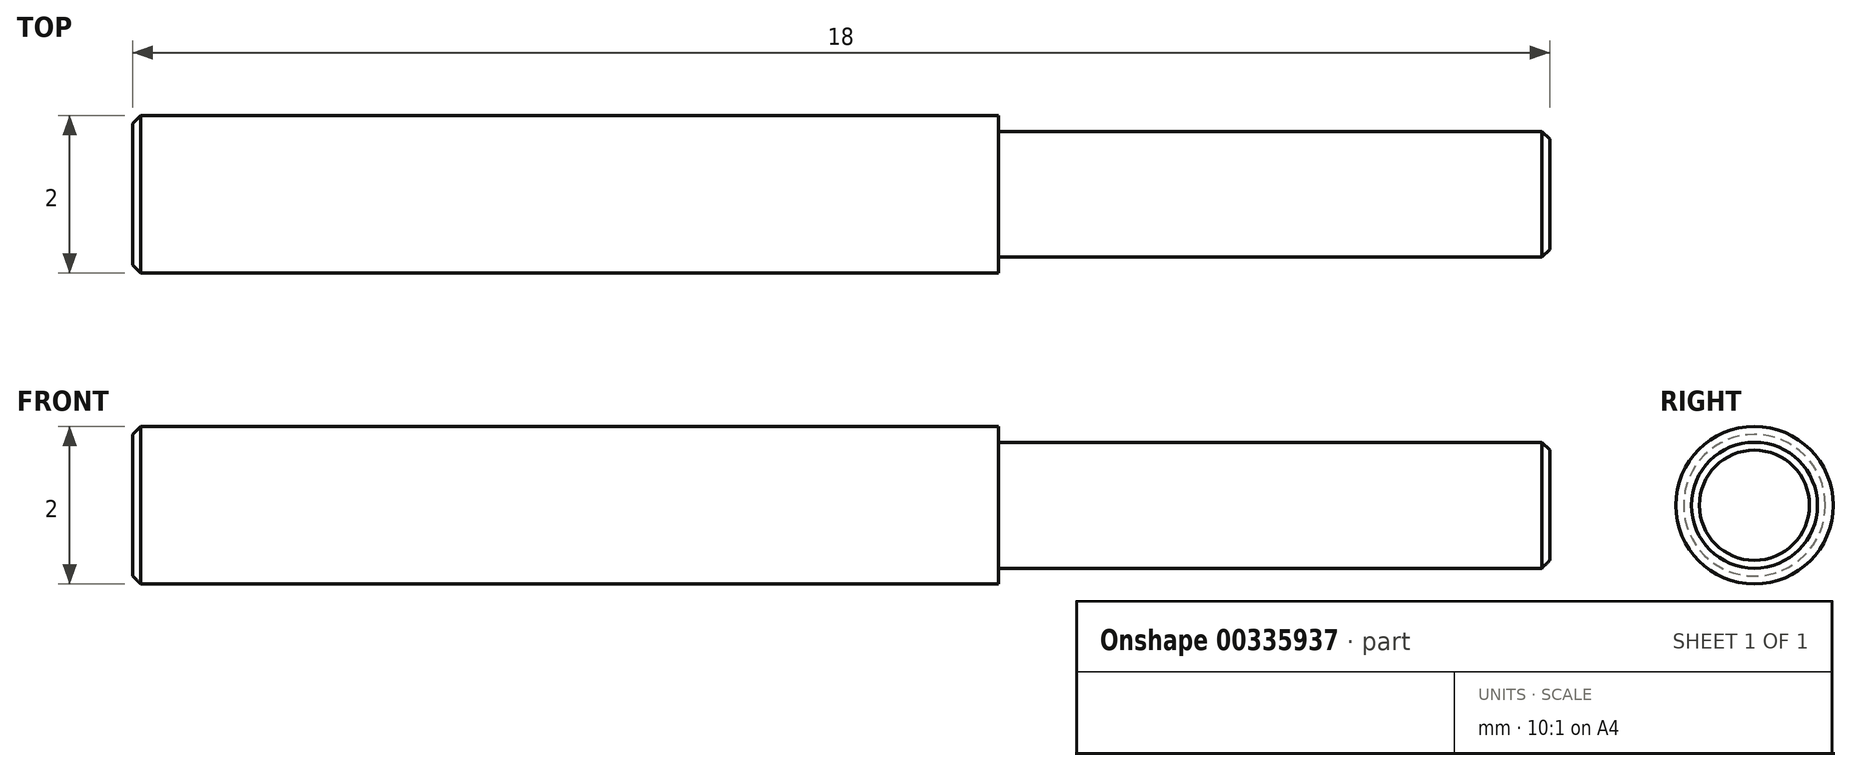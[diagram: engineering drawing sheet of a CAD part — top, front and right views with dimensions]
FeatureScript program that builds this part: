
annotation { "Feature Type Name" : "Feature", "Feature Type Description" : "" }
export const myFeature = defineFeature(function(context is Context, id is Id, definition is map)
    precondition{}
    {
        {
            var Q0;
            Q0=qCreatedBy(makeId("Front.planeOp"),FACE);
            var sketch = newSketch(context, id + "F0", { "sketchPlane" : qUnion([Q0])});
            skLineSegment(sketch, "E0.bottom", {"start": v(-11, 1) * mm, "end": v(0, 1) * mm});
            skLineSegment(sketch, "E0.top", {"start": v(-11, -1) * mm, "end": v(0, -1) * mm});
            skLineSegment(sketch, "E0.left", {"start": v(-11, 1) * mm, "end": v(-11, -1) * mm});
            skLineSegment(sketch, "E0.right", {"start": v(0, 1) * mm, "end": v(0, -1) * mm});
            skLineSegment(sketch, "E1.bottom", {"start": v(0, 0.8) * mm, "end": v(7, 0.8) * mm});
            skLineSegment(sketch, "E1.top", {"start": v(0, -0.8) * mm, "end": v(7, -0.8) * mm});
            skLineSegment(sketch, "E1.left", {"start": v(0, 0.8) * mm, "end": v(0, -0.8) * mm});
            skLineSegment(sketch, "E1.right", {"start": v(7, 0.8) * mm, "end": v(7, -0.8) * mm});
            skPoint(sketch, "E2", {"position": v(0, 0) * mm});
            skLineSegment(sketch, "E3", {"start": v(-11, 0) * mm, "end": v(7, 0) * mm});
            skSolve(sketch);
        }
        {
            var Q0;
            {var subQ5=sQuery(id+"F0.wireOp",EDGE,"E0.bottom");Q0=makeQuery(id+"F0.imprint","IMPRINT",FACE,{"disambiguationData":[TD([[makeQuery(id+"F0.imprint","IMPRINT",EDGE,{"derivedFrom":subQ5}),-1.0]])]});}
            var Q1;
            {var subQ0=sQuery(id+"F0.wireOp",EDGE,"E1.bottom");Q1=makeQuery(id+"F0.imprint","IMPRINT",FACE,{"disambiguationData":[TD([[makeQuery(id+"F0.imprint","IMPRINT",EDGE,{"derivedFrom":subQ0}),-1.0]])]});}
            var Q2;
            Q2=sQuery(id+"F0.wireOp",EDGE,"E3");
            revolve(context, id + "F1", {"entities" : qUnion([Q0, Q1]), "axis" : qUnion([Q2]), "revolveType" : RevolveType.FULL});
        }
        {
            var Q0;
            Q0=makeQuery(id+"F1.opRevolve","SWEPT_EDGE",EDGE,{"disambiguationData":[OSD([sQuery(id+"F0.wireOp",EDGE,"E0.bottom"),sQuery(id+"F0.wireOp",EDGE,"E0.left")])]});
            var Q1;
            Q1=makeQuery(id+"F1.opRevolve","SWEPT_EDGE",EDGE,{"disambiguationData":[OSD([sQuery(id+"F0.wireOp",EDGE,"E1.bottom"),sQuery(id+"F0.wireOp",EDGE,"E1.right")])]});
            chamfer(context, id + "F2", {"entities" : qUnion([Q0, Q1]), "width" : 0.1 * mm, "tangentPropagation" : true});
        }
    });
